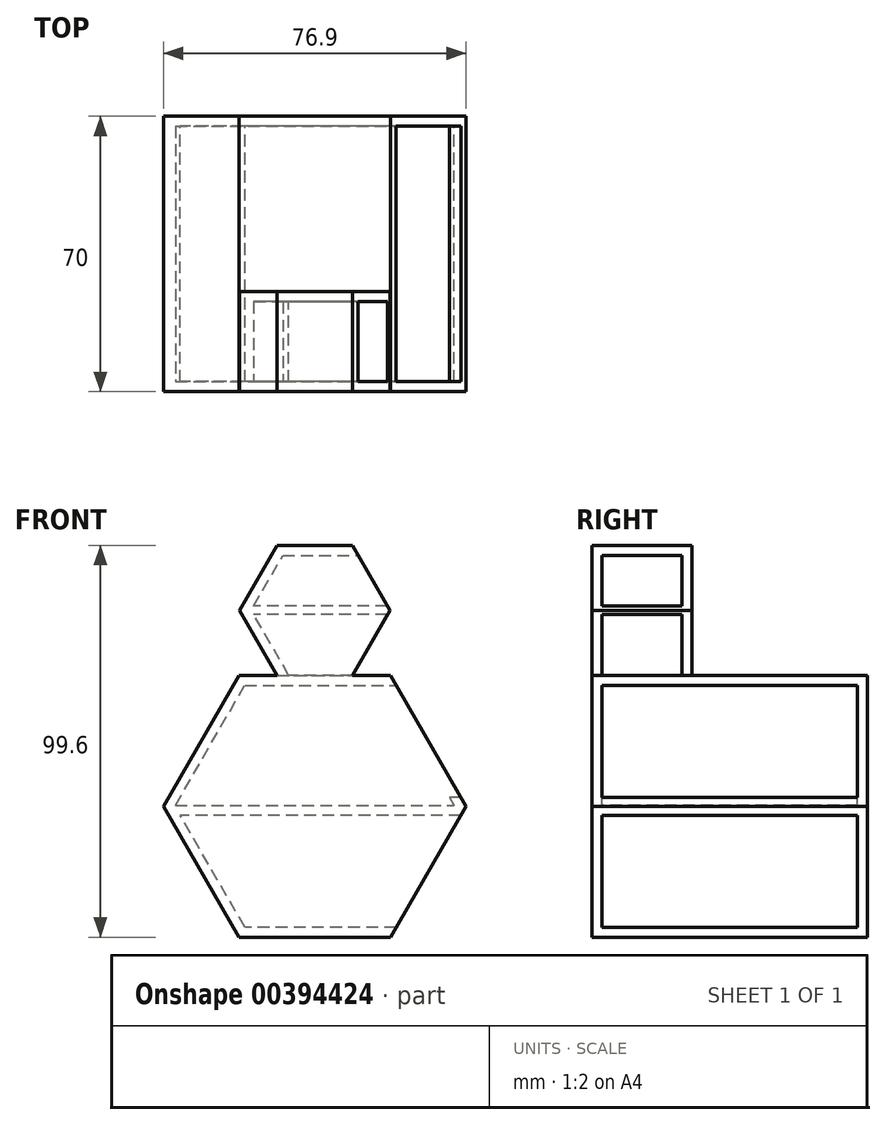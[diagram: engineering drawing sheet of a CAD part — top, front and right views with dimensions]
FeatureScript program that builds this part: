
annotation { "Feature Type Name" : "Feature", "Feature Type Description" : "" }
export const myFeature = defineFeature(function(context is Context, id is Id, definition is map)
    precondition{}
    {
        {
            var Q0;
            Q0=qCreatedBy(makeId("Front.planeOp"),FACE);
            var sketch = newSketch(context, id + "F0", { "sketchPlane" : qUnion([Q0])});
            skCircle(sketch, "E0.cCircle", {"center": v(0, 0) * mm, "radius": 33.3 * mm, "construction": true});
            skLineSegment(sketch, "E0.0", {"start": v(-19.22, 33.3) * mm, "end": v(19.22, 33.3) * mm});
            skLineSegment(sketch, "E0.1", {"start": v(19.22, 33.3) * mm, "end": v(38.45, 0) * mm});
            skLineSegment(sketch, "E0.2", {"start": v(38.45, 0) * mm, "end": v(19.22, -33.3) * mm});
            skLineSegment(sketch, "E0.3", {"start": v(19.22, -33.3) * mm, "end": v(-19.22, -33.3) * mm});
            skLineSegment(sketch, "E0.4", {"start": v(-19.22, -33.3) * mm, "end": v(-38.45, 0) * mm});
            skLineSegment(sketch, "E0.5", {"start": v(-38.45, 0) * mm, "end": v(-19.22, 33.3) * mm});
            skPoint(sketch, "E0.0.midPoint", {"position": v(0, 33.3) * mm});
            skSolve(sketch);
        }
        {
            var Q0;
            Q0=makeQuery(id+"F0.imprint","IMPRINT",FACE,{"disambiguationData":[TD([[makeQuery(id+"F0.imprint","IMPRINT",EDGE,{"derivedFrom":sQuery(id+"F0.wireOp",EDGE,"E0.0")}),-1.0]])]});
            extrude(context, id + "F1", {"entities" : qUnion([Q0]), "depth" : 70 * mm});
        }
        {
            var Q0;
            Q0=makeQuery(id+"F1.opExtrude","SWEPT_FACE",FACE,{"disambiguationData":[OSD([sQuery(id+"F0.wireOp",EDGE,"E0.1")])]});
            var Q1;
            Q1=makeQuery(id+"F1.opExtrude","SWEPT_FACE",FACE,{"disambiguationData":[OSD([sQuery(id+"F0.wireOp",EDGE,"E0.2")])]});
            shell(context, id + "F2", {"entities" : qUnion([Q0, Q1]), "thickness" : 2.54 * mm});
        }
        {
            var Q0;
            Q0=makeQuery(id+"F1.opExtrude","CAP_FACE",FACE,{"disambiguationData":[OSD([sQuery(id+"F0.wireOp",EDGE,"E0.0"),sQuery(id+"F0.wireOp",EDGE,"E0.1"),sQuery(id+"F0.wireOp",EDGE,"E0.2"),sQuery(id+"F0.wireOp",EDGE,"E0.3"),sQuery(id+"F0.wireOp",EDGE,"E0.4"),sQuery(id+"F0.wireOp",EDGE,"E0.5")])],"isStart":false});
            var sketch = newSketch(context, id + "F3", { "sketchPlane" : qUnion([Q0])});
            skLineSegment(sketch, "E1", {"start": v(0, 33.3) * mm, "end": v(0, 66.31) * mm, "construction": true});
            skCircle(sketch, "E2.cCircle", {"center": v(0, 49.8) * mm, "radius": 16.51 * mm, "construction": true});
            skLineSegment(sketch, "E2.0", {"start": v(9.53, 33.3) * mm, "end": v(-9.53, 33.3) * mm});
            skLineSegment(sketch, "E2.1", {"start": v(-9.53, 33.3) * mm, "end": v(-19.06, 49.8) * mm});
            skLineSegment(sketch, "E2.2", {"start": v(-19.06, 49.8) * mm, "end": v(-9.53, 66.31) * mm});
            skLineSegment(sketch, "E2.3", {"start": v(-9.53, 66.31) * mm, "end": v(9.53, 66.31) * mm});
            skLineSegment(sketch, "E2.4", {"start": v(9.53, 66.31) * mm, "end": v(19.06, 49.8) * mm});
            skLineSegment(sketch, "E2.5", {"start": v(19.06, 49.8) * mm, "end": v(9.53, 33.3) * mm});
            skPoint(sketch, "E2.0.midPoint", {"position": v(0, 33.3) * mm});
            skSolve(sketch);
        }
        {
            var Q0;
            Q0=makeQuery(id+"F3.imprint","IMPRINT",FACE,{"disambiguationData":[TD([[makeQuery(id+"F3.imprint","IMPRINT",EDGE,{"derivedFrom":sQuery(id+"F3.wireOp",EDGE,"E2.0")}),1.0]])]});
            extrude(context, id + "F4", {"entities" : qUnion([Q0]), "operationType" : NewBodyOperationType.ADD, "oppositeDirection" : true, "depth" : 25.4 * mm});
        }
        {
            var Q0;
            Q0=makeQuery(id+"F4.boolean.opBoolean","MERGE",FACE,{"derivedFrom":[makeQuery(id+"F1.opExtrude","CAP_FACE",FACE,{"disambiguationData":[OSD([sQuery(id+"F0.wireOp",EDGE,"E0.0"),sQuery(id+"F0.wireOp",EDGE,"E0.1"),sQuery(id+"F0.wireOp",EDGE,"E0.2"),sQuery(id+"F0.wireOp",EDGE,"E0.3"),sQuery(id+"F0.wireOp",EDGE,"E0.4"),sQuery(id+"F0.wireOp",EDGE,"E0.5")])],"isStart":false}),makeQuery(id+"F4.opExtrude","CAP_FACE",FACE,{"disambiguationData":[OSD([sQuery(id+"F3.wireOp",EDGE,"E2.0"),sQuery(id+"F3.wireOp",EDGE,"E2.1"),sQuery(id+"F3.wireOp",EDGE,"E2.2"),sQuery(id+"F3.wireOp",EDGE,"E2.3"),sQuery(id+"F3.wireOp",EDGE,"E2.4"),sQuery(id+"F3.wireOp",EDGE,"E2.5")])],"isStart":true})]});
            var sketch = newSketch(context, id + "F5", { "sketchPlane" : qUnion([Q0])});
            skLineSegment(sketch, "E3.bottom", {"start": v(37.12, 2.3) * mm, "end": v(-37.12, 2.3) * mm});
            skLineSegment(sketch, "E3.top", {"start": v(37.12, -2.3) * mm, "end": v(-37.12, -2.3) * mm});
            skPoint(sketch, "E3.middle", {"position": v(0, 0) * mm});
            skLineSegment(sketch, "E4", {"start": v(37.12, 2.3) * mm, "end": v(38.45, 0) * mm});
            skLineSegment(sketch, "E5", {"start": v(38.45, 0) * mm, "end": v(37.12, -2.3) * mm});
            skPoint(sketch, "E6.orphan", {"position": v(38.45, 2.3) * mm});
            skPoint(sketch, "E7.orphan", {"position": v(38.45, -2.3) * mm});
            skLineSegment(sketch, "E8", {"start": v(-37.12, 2.3) * mm, "end": v(-38.45, 0) * mm});
            skLineSegment(sketch, "E9", {"start": v(-38.45, 0) * mm, "end": v(-37.12, -2.3) * mm});
            skPoint(sketch, "E10.orphan", {"position": v(-38.45, -2.3) * mm});
            skPoint(sketch, "E11.orphan", {"position": v(-38.45, 2.3) * mm});
            skSolve(sketch);
        }
        {
            var Q0;
            Q0 = qSketchRegion(id + "F5", true);
            var Q1;
            Q1=makeQuery(id+"F1.opExtrude","CAP_FACE",FACE,{"disambiguationData":[OSD([sQuery(id+"F0.wireOp",EDGE,"E0.0"),sQuery(id+"F0.wireOp",EDGE,"E0.1"),sQuery(id+"F0.wireOp",EDGE,"E0.2"),sQuery(id+"F0.wireOp",EDGE,"E0.3"),sQuery(id+"F0.wireOp",EDGE,"E0.4"),sQuery(id+"F0.wireOp",EDGE,"E0.5")])],"isStart":true});
            extrude(context, id + "F6", {"entities" : qUnion([Q0]), "operationType" : NewBodyOperationType.ADD, "endBound" : BoundingType.UP_TO_SURFACE, "oppositeDirection" : true, "endBoundEntityFace" : qUnion([Q1]), "depth" : 25.4 * mm});
        }
        {
            var Q0;
            Q0=makeQuery(id+"F6.opExtrude","SWEPT_FACE",FACE,{"disambiguationData":[OSD([sQuery(id+"F5.wireOp",EDGE,"E3.bottom")])]});
            var Q1;
            Q1=makeQuery(id+"F4.opExtrude","SWEPT_FACE",FACE,{"disambiguationData":[OSD([sQuery(id+"F3.wireOp",EDGE,"E2.5")])]});
            shell(context, id + "F7", {"entities" : qUnion([Q0, Q1]), "thickness" : 2.54 * mm});
        }
        {
            var Q0;
            Q0=makeQuery(id+"F4.opExtrude","SWEPT_FACE",FACE,{"disambiguationData":[OSD([sQuery(id+"F3.wireOp",EDGE,"E2.5")])]});
            var Q1;
            Q1=makeQuery(id+"F4.opExtrude","SWEPT_FACE",FACE,{"disambiguationData":[OSD([sQuery(id+"F3.wireOp",EDGE,"E2.4")])]});
            shell(context, id + "F8", {"entities" : qUnion([Q0, Q1]), "thickness" : 2.54 * mm});
        }
        {
            var Q0;
            Q0=makeQuery(id+"F4.boolean.opBoolean","MERGE",FACE,{"derivedFrom":[makeQuery(id+"F1.opExtrude","CAP_FACE",FACE,{"disambiguationData":[OSD([sQuery(id+"F0.wireOp",EDGE,"E0.0"),sQuery(id+"F0.wireOp",EDGE,"E0.1"),sQuery(id+"F0.wireOp",EDGE,"E0.2"),sQuery(id+"F0.wireOp",EDGE,"E0.3"),sQuery(id+"F0.wireOp",EDGE,"E0.4"),sQuery(id+"F0.wireOp",EDGE,"E0.5")])],"isStart":false}),makeQuery(id+"F4.opExtrude","CAP_FACE",FACE,{"disambiguationData":[OSD([sQuery(id+"F3.wireOp",EDGE,"E2.0"),sQuery(id+"F3.wireOp",EDGE,"E2.1"),sQuery(id+"F3.wireOp",EDGE,"E2.2"),sQuery(id+"F3.wireOp",EDGE,"E2.3"),sQuery(id+"F3.wireOp",EDGE,"E2.4"),sQuery(id+"F3.wireOp",EDGE,"E2.5")])],"isStart":true})]});
            var sketch = newSketch(context, id + "F9", { "sketchPlane" : qUnion([Q0])});
            skLineSegment(sketch, "E12.bottom", {"start": v(18.43, 50.9) * mm, "end": v(-18.43, 50.9) * mm});
            skLineSegment(sketch, "E12.top", {"start": v(18.43, 48.71) * mm, "end": v(-18.43, 48.71) * mm});
            skPoint(sketch, "E12.middle", {"position": v(0, 49.8) * mm});
            skLineSegment(sketch, "E13", {"start": v(18.43, 50.9) * mm, "end": v(19.06, 49.8) * mm});
            skLineSegment(sketch, "E14", {"start": v(19.06, 49.8) * mm, "end": v(18.43, 48.71) * mm});
            skPoint(sketch, "E15.orphan", {"position": v(19.06, 50.9) * mm});
            skPoint(sketch, "E16.orphan", {"position": v(19.06, 48.71) * mm});
            skLineSegment(sketch, "E17", {"start": v(-18.43, 50.9) * mm, "end": v(-19.06, 49.8) * mm});
            skLineSegment(sketch, "E18", {"start": v(-19.06, 49.8) * mm, "end": v(-18.43, 48.71) * mm});
            skPoint(sketch, "E19.orphan", {"position": v(-19.06, 50.9) * mm});
            skPoint(sketch, "E20.orphan", {"position": v(-19.06, 48.71) * mm});
            skSolve(sketch);
        }
        {
            var Q0;
            Q0 = qSketchRegion(id + "F9", true);
            var Q1;
            Q1=makeQuery(id+"F4.opExtrude","CAP_FACE",FACE,{"disambiguationData":[OSD([sQuery(id+"F3.wireOp",EDGE,"E2.0"),sQuery(id+"F3.wireOp",EDGE,"E2.1"),sQuery(id+"F3.wireOp",EDGE,"E2.2"),sQuery(id+"F3.wireOp",EDGE,"E2.3"),sQuery(id+"F3.wireOp",EDGE,"E2.4"),sQuery(id+"F3.wireOp",EDGE,"E2.5")])],"isStart":false});
            extrude(context, id + "F10", {"entities" : qUnion([Q0]), "operationType" : NewBodyOperationType.ADD, "endBound" : BoundingType.UP_TO_SURFACE, "oppositeDirection" : true, "endBoundEntityFace" : qUnion([Q1]), "depth" : 25.4 * mm});
        }
    });
